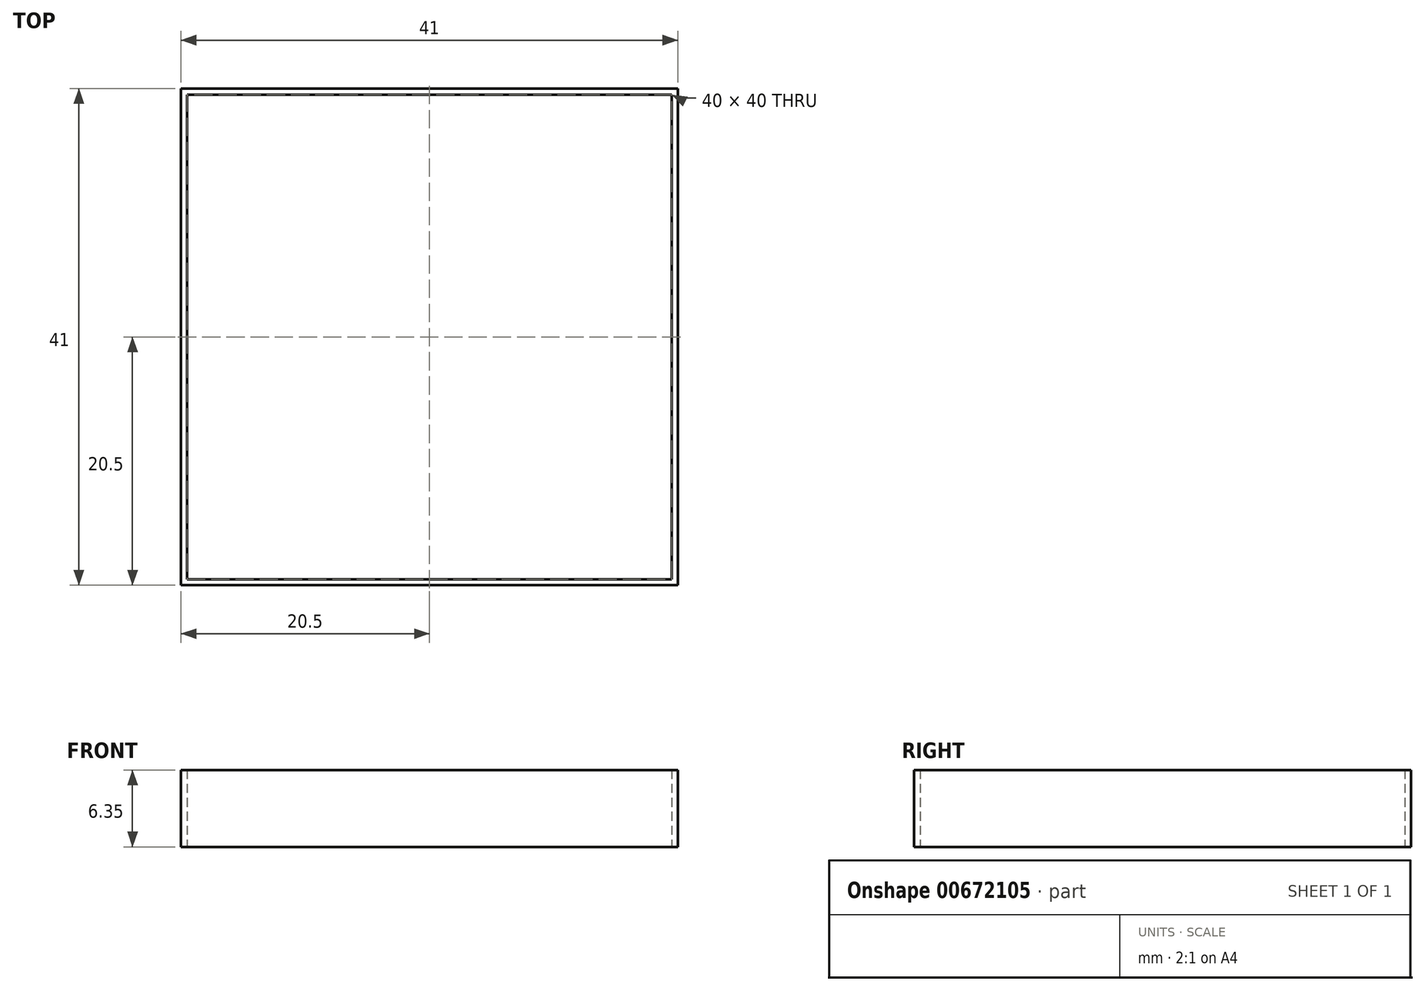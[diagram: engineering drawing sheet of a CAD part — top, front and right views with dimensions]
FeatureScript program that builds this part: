
annotation { "Feature Type Name" : "Feature", "Feature Type Description" : "" }
export const myFeature = defineFeature(function(context is Context, id is Id, definition is map)
    precondition{}
    {
        {
            var Q0;
            Q0=qCreatedBy(makeId("Top.planeOp"),FACE);
            var sketch = newSketch(context, id + "F0", { "sketchPlane" : qUnion([Q0])});
            skLineSegment(sketch, "E0.bottom", {"start": v(20.5, 20.5) * mm, "end": v(-20.5, 20.5) * mm});
            skLineSegment(sketch, "E0.top", {"start": v(20.5, -20.5) * mm, "end": v(-20.5, -20.5) * mm});
            skLineSegment(sketch, "E0.left", {"start": v(20.5, 20.5) * mm, "end": v(20.5, -20.5) * mm});
            skLineSegment(sketch, "E0.right", {"start": v(-20.5, 20.5) * mm, "end": v(-20.5, -20.5) * mm});
            skPoint(sketch, "E0.middle", {"position": v(0, 0) * mm});
            skLineSegment(sketch, "E1.bottom", {"start": v(20, 20) * mm, "end": v(-20, 20) * mm});
            skLineSegment(sketch, "E1.top", {"start": v(20, -20) * mm, "end": v(-20, -20) * mm});
            skLineSegment(sketch, "E1.left", {"start": v(20, 20) * mm, "end": v(20, -20) * mm});
            skLineSegment(sketch, "E1.right", {"start": v(-20, 20) * mm, "end": v(-20, -20) * mm});
            skSolve(sketch);
        }
        {
            var Q0;
            Q0=makeQuery(id+"F0.imprint","IMPRINT",FACE,{"disambiguationData":[TD([[makeQuery(id+"F0.imprint","IMPRINT",EDGE,{"derivedFrom":sQuery(id+"F0.wireOp",EDGE,"E0.bottom")}),1.0]])]});
            extrude(context, id + "F1", {"entities" : qUnion([Q0]), "depth" : 6.35 * mm, "offsetDistance" : 25.4 * mm});
        }
        {
            var Q0;
            Q0=qCreatedBy(makeId("Right.planeOp"),FACE);
            var sketch = newSketch(context, id + "F2", { "sketchPlane" : qUnion([Q0])});
            skLineSegment(sketch, "E2", {"start": v(-20, 0) * mm, "end": v(-12.48, -26.3) * mm});
            skLineSegment(sketch, "E3", {"start": v(20.5, 0) * mm, "end": v(20.5, -8.43) * mm});
            skLineSegment(sketch, "E4", {"start": v(20.5, -8.43) * mm, "end": v(-6.12, -22.82) * mm});
            skSolve(sketch);
        }
        {
            var Q0;
            Q0=sQuery(id+"F2.wireOp",EDGE,"E4");
            var Q1;
            Q1=sQuery(id+"F2.wireOp",EDGE,"E3");
            var Q2;
            Q2=sQuery(id+"F2.wireOp",EDGE,"E2");
            extrude(context, id + "F3", {"bodyType" : ToolBodyType.SURFACE, "surfaceEntities" : qUnion([Q0, Q1, Q2]), "depth" : 20.5 * mm, "offsetDistance" : 25.4 * mm});
        }
        {
            var Q0;
            Q0 = qSketchRegion(id + "F2", true);
            var Q1;
            Q1 = qConstructionFilter(qBodyType(qCreatedBy(id + "F2" ,EDGE), BodyType.WIRE), ConstructionObject.NO);
            extrude(context, id + "F4", {"entities" : qUnion([Q0]), "bodyType" : ToolBodyType.SURFACE, "surfaceEntities" : qUnion([Q1]), "oppositeDirection" : true, "depth" : 20.5 * mm, "offsetDistance" : 25.4 * mm});
        }
    });
